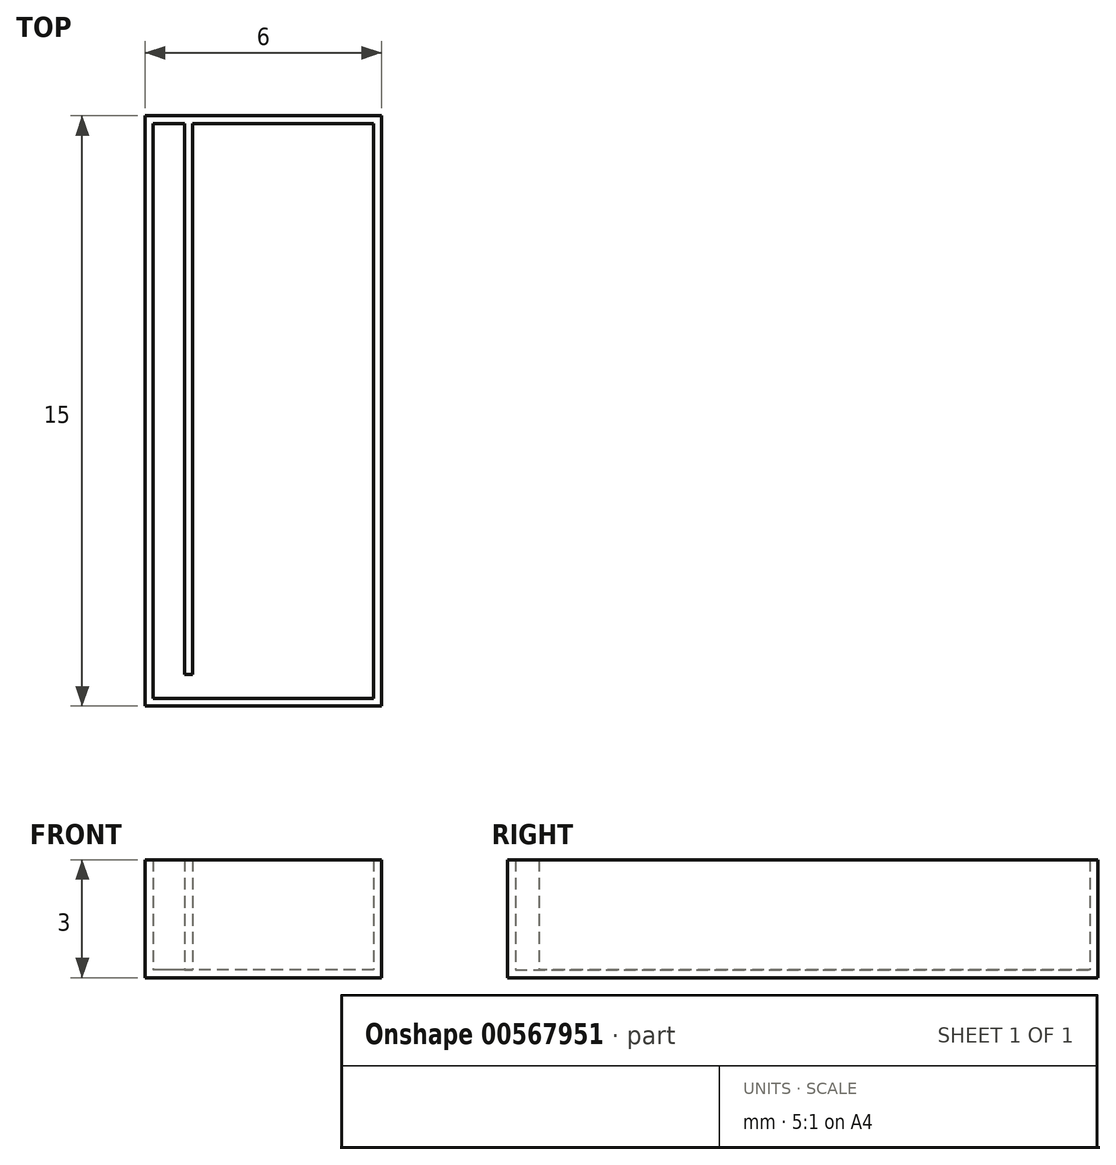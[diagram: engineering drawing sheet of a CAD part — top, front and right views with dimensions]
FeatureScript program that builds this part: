
annotation { "Feature Type Name" : "Feature", "Feature Type Description" : "" }
export const myFeature = defineFeature(function(context is Context, id is Id, definition is map)
    precondition{}
    {
        {
            var Q0;
            Q0=qCreatedBy(makeId("Top.planeOp"),FACE);
            var sketch = newSketch(context, id + "F0", { "sketchPlane" : qUnion([Q0])});
            skLineSegment(sketch, "E0.bottom", {"start": v(3, -7.5) * mm, "end": v(-3, -7.5) * mm});
            skLineSegment(sketch, "E0.top", {"start": v(3, 7.5) * mm, "end": v(-3, 7.5) * mm});
            skLineSegment(sketch, "E0.left", {"start": v(3, -7.5) * mm, "end": v(3, 7.5) * mm});
            skLineSegment(sketch, "E0.right", {"start": v(-3, -7.5) * mm, "end": v(-3, 7.5) * mm});
            skPoint(sketch, "E0.middle", {"position": v(0, 0) * mm});
            skSolve(sketch);
        }
        {
            var Q0;
            Q0=makeQuery(id+"F0.imprint","IMPRINT",FACE,{"disambiguationData":[TD([[makeQuery(id+"F0.imprint","IMPRINT",EDGE,{"derivedFrom":sQuery(id+"F0.wireOp",EDGE,"E0.bottom")}),-1.0]])]});
            extrude(context, id + "F1", {"entities" : qUnion([Q0]), "depth" : 3 * mm, "offsetDistance" : 25 * mm});
        }
        {
            var Q0;
            Q0=makeQuery(id+"F1.opExtrude","CAP_FACE",FACE,{"disambiguationData":[OSD([sQuery(id+"F0.wireOp",EDGE,"E0.bottom"),sQuery(id+"F0.wireOp",EDGE,"E0.top"),sQuery(id+"F0.wireOp",EDGE,"E0.left"),sQuery(id+"F0.wireOp",EDGE,"E0.right")])],"isStart":false});
            shell(context, id + "F2", {"entities" : qUnion([Q0]), "thickness" : 0.2 * mm});
        }
        {
            var Q0;
            Q0=makeQuery(id+"F2.opShell","OFFSET_FACE",FACE,{"disambiguationData":[OSD([sQuery(id+"F0.wireOp",EDGE,"E0.bottom"),sQuery(id+"F0.wireOp",EDGE,"E0.top"),sQuery(id+"F0.wireOp",EDGE,"E0.left"),sQuery(id+"F0.wireOp",EDGE,"E0.right")])]});
            var sketch = newSketch(context, id + "F3", { "sketchPlane" : qUnion([Q0])});
            skLineSegment(sketch, "E1.bottom", {"start": v(-2, 7.3) * mm, "end": v(-1.8, 7.3) * mm});
            skLineSegment(sketch, "E1.top", {"start": v(-2, -6.7) * mm, "end": v(-1.8, -6.7) * mm});
            skLineSegment(sketch, "E1.left", {"start": v(-2, 7.3) * mm, "end": v(-2, -6.7) * mm});
            skLineSegment(sketch, "E1.right", {"start": v(-1.8, 7.3) * mm, "end": v(-1.8, -6.7) * mm});
            skSolve(sketch);
        }
        {
            var Q0;
            Q0 = qSketchRegion(id + "F3", true);
            extrude(context, id + "F4", {"entities" : qUnion([Q0]), "operationType" : NewBodyOperationType.ADD, "depth" : 2.8 * mm, "offsetDistance" : 25 * mm});
        }
    });
